# Revit family: Fittings_CapillaryW1ReducerCoupling_Ardent_REECE
name_source: partatom
category: Pipe Fittings
units: mm (PartAtom-declared; Revit-internal decimal feet)

## family parameters
Always vertical = Yes
Cut with Voids When Loaded = No
OmniClass Number = 23.60.30.11.14
OmniClass Title = Pipework Fittings
Part Type = Transition
Round Connector Dimension = Use Diameter
Shared = No
Work Plane-Based = No

## types (1)
- Fittings_CapillaryW1ReducerCoupling_Ardent_REECE
    Description = TBC
    FittingType = ReducerCoupling
    Lookup Table Name = Fittings_CapillaryW1ReducerCoupling_Ardent_REECE
    Manufacturer = Reece
    Material = Reece_Copper
    Model = Ardent Capillary W1R Reducer Coupling
    ModifiedIssue_ANZRS = 20151012.54 $
    Type Comments = Manufactured to comply and marked in accordance with Australian Standards AS1432 and AS3688
    URL = http://www.reece.com.au

## geometry (parser evidence)
native form markers: Blend x2, Sweep x3
no freeform markers — native parametric forms only
